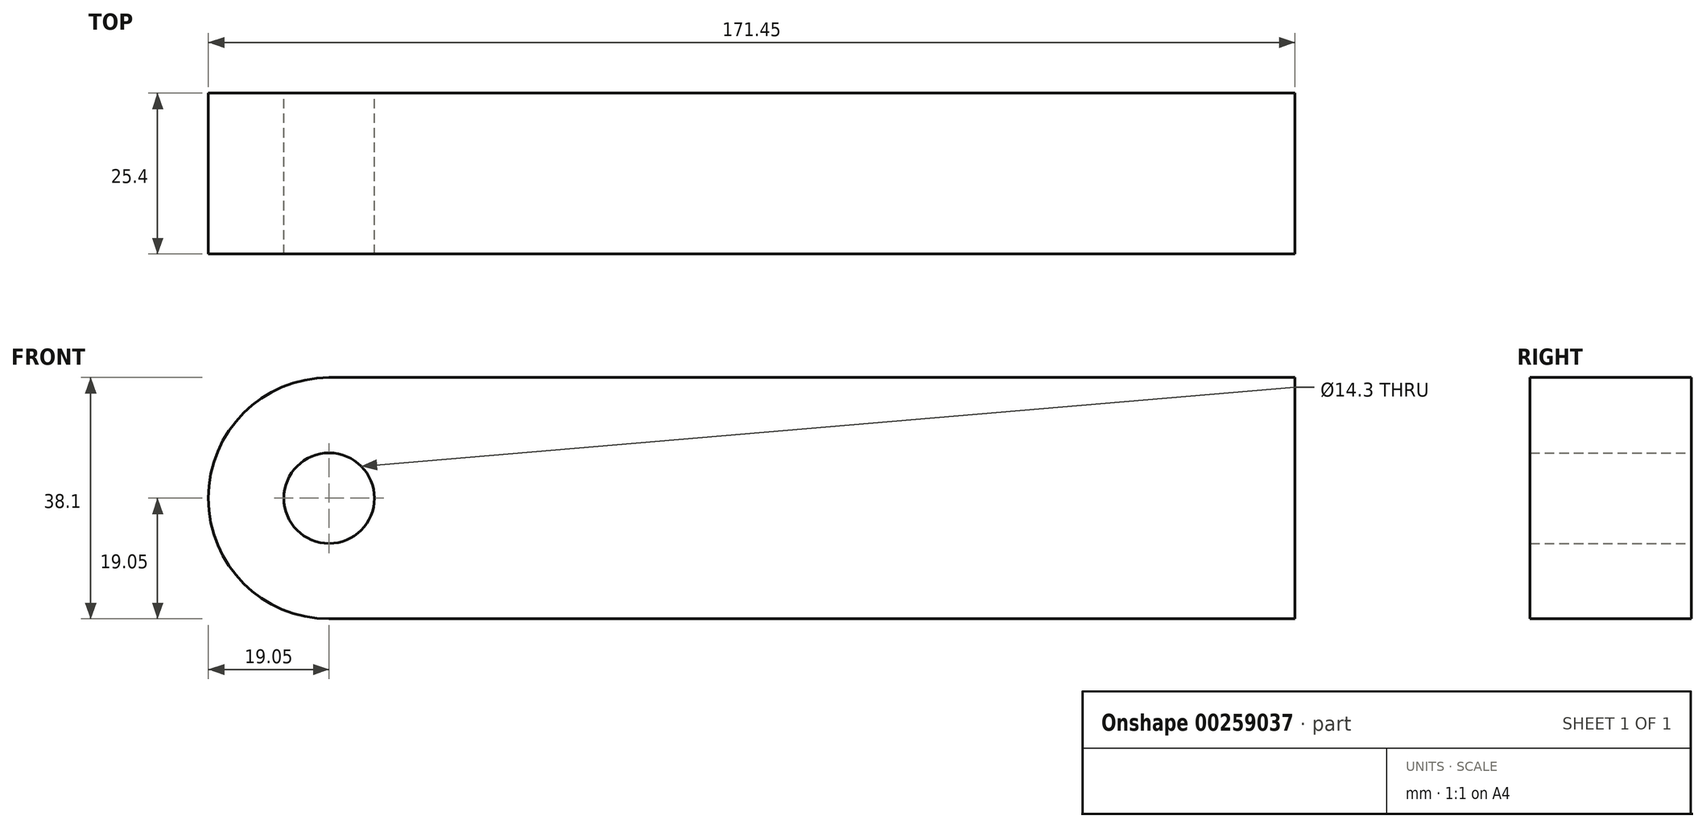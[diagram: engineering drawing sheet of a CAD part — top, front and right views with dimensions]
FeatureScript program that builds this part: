
annotation { "Feature Type Name" : "Feature", "Feature Type Description" : "" }
export const myFeature = defineFeature(function(context is Context, id is Id, definition is map)
    precondition{}
    {
        {
            var Q0;
            Q0=qCreatedBy(makeId("Front.planeOp"),FACE);
            var sketch = newSketch(context, id + "F0", { "sketchPlane" : qUnion([Q0])});
            skCircle(sketch, "E0", {"center": v(0, 0) * mm, "radius": 19.05 * mm});
            skCircle(sketch, "E1", {"center": v(0, 0) * mm, "radius": 7.15 * mm});
            skLineSegment(sketch, "E2.bottom", {"start": v(0, 19.05) * mm, "end": v(152.4, 19.05) * mm});
            skLineSegment(sketch, "E2.top", {"start": v(0, -19.05) * mm, "end": v(152.4, -19.05) * mm});
            skLineSegment(sketch, "E2.left", {"start": v(0, 19.05) * mm, "end": v(0, -19.05) * mm});
            skLineSegment(sketch, "E2.right", {"start": v(152.4, 19.05) * mm, "end": v(152.4, -19.05) * mm});
            skSolve(sketch);
        }
        {
            var Q0;
            {var subQ0=sQuery(id+"F0.wireOp",EDGE,"E2.left");var subQ4=sQuery(id+"F0.wireOp",EDGE,"E1");var subQ5=makeQuery(id+"F0.imprint","INTERSECT",VERTEX,{"disambiguationData":[OD(0.0)],"derivedFrom":[subQ4,subQ0]});Q0=makeQuery(id+"F0.imprint","IMPRINT",FACE,{"disambiguationData":[TD([[makeQuery(id+"F0.imprint","IMPRINT",EDGE,{"disambiguationData":[TD([[subQ5,1.0]])],"derivedFrom":subQ4}),-1.0]])]});}
            var Q1;
            {var subQ0=sQuery(id+"F0.wireOp",EDGE,"E2.left");var subQ4=sQuery(id+"F0.wireOp",EDGE,"E1");var subQ5=makeQuery(id+"F0.imprint","INTERSECT",VERTEX,{"disambiguationData":[OD(0.0)],"derivedFrom":[subQ4,subQ0]});Q1=makeQuery(id+"F0.imprint","IMPRINT",FACE,{"disambiguationData":[TD([[makeQuery(id+"F0.imprint","IMPRINT",EDGE,{"disambiguationData":[TD([[subQ5,-1.0]])],"derivedFrom":subQ4}),-1.0]])]});}
            var Q2;
            {var subQ1=sQuery(id+"F0.wireOp",EDGE,"E2.bottom");Q2=makeQuery(id+"F0.imprint","IMPRINT",FACE,{"disambiguationData":[TD([[makeQuery(id+"F0.imprint","IMPRINT",EDGE,{"derivedFrom":subQ1}),-1.0]])]});}
            extrude(context, id + "F1", {"entities" : qUnion([Q0, Q1, Q2]), "depth" : 25.4 * mm});
        }
    });
